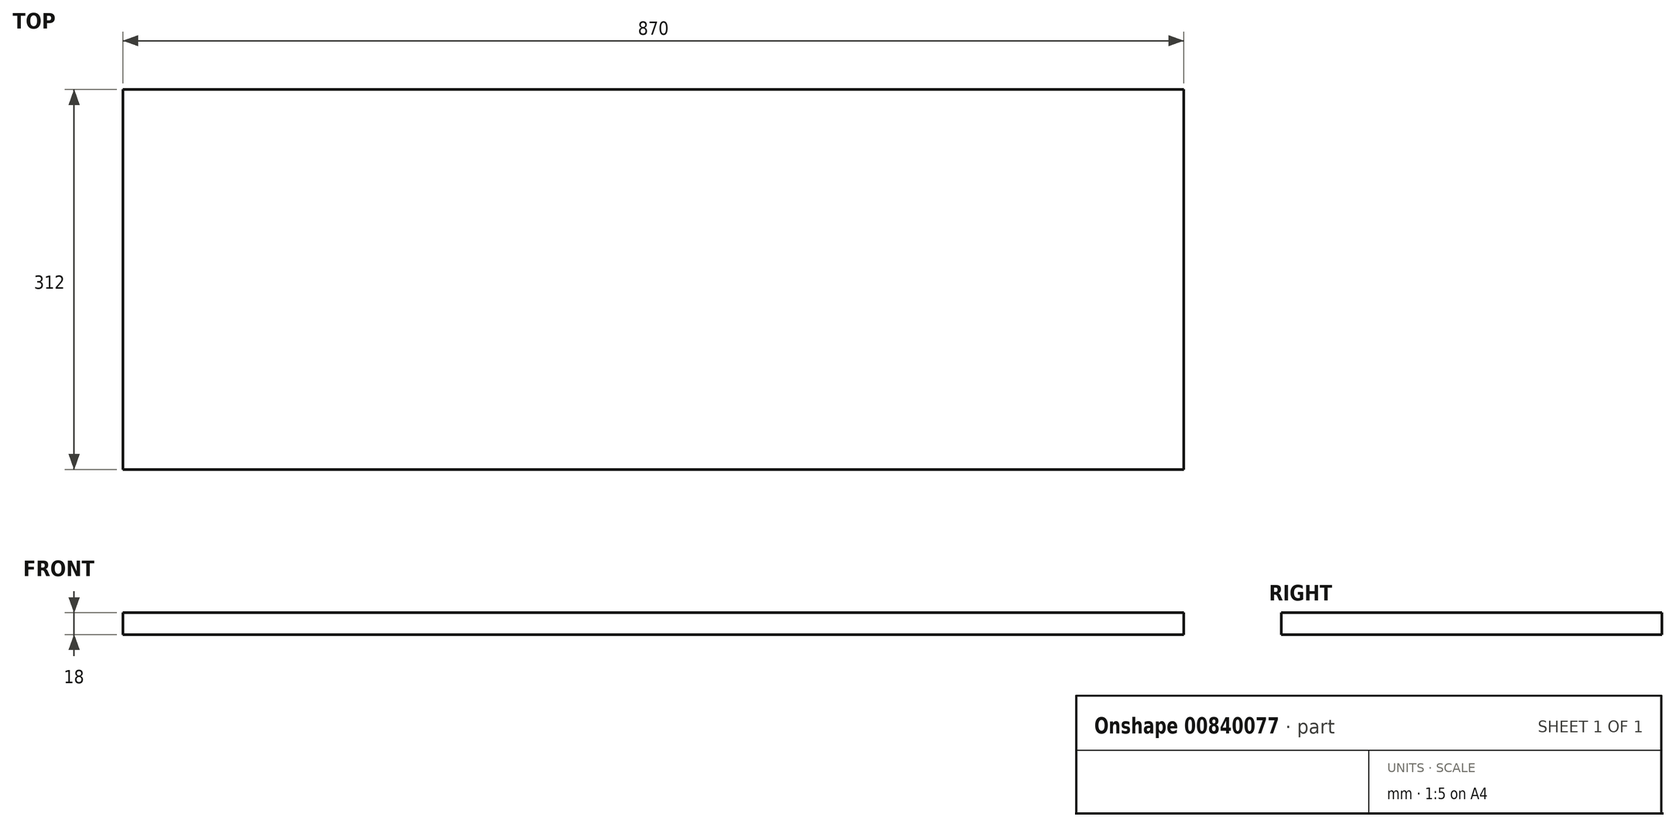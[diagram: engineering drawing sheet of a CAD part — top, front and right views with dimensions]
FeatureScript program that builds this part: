
annotation { "Feature Type Name" : "Feature", "Feature Type Description" : "" }
export const myFeature = defineFeature(function(context is Context, id is Id, definition is map)
    precondition{}
    {
        {
            var Q0;
            Q0=qCreatedBy(makeId("Top.planeOp"),FACE);
            var sketch = newSketch(context, id + "F0", { "sketchPlane" : qUnion([Q0])});
            skLineSegment(sketch, "E0.bottom", {"start": v(-435, 156) * mm, "end": v(435, 156) * mm});
            skLineSegment(sketch, "E0.top", {"start": v(-435, -156) * mm, "end": v(435, -156) * mm});
            skLineSegment(sketch, "E0.left", {"start": v(-435, 156) * mm, "end": v(-435, -156) * mm});
            skLineSegment(sketch, "E0.right", {"start": v(435, 156) * mm, "end": v(435, -156) * mm});
            skLineSegment(sketch, "E1", {"start": v(-435, 156) * mm, "end": v(435, -156) * mm, "construction": true});
            skSolve(sketch);
        }
        {
            var Q0;
            Q0=qSketchRegion(id+"F0",true);
            extrude(context, id + "F1", {"entities" : qUnion([Q0]), "depth" : 18 * mm, "offsetDistance" : 25 * mm});
        }
    });
